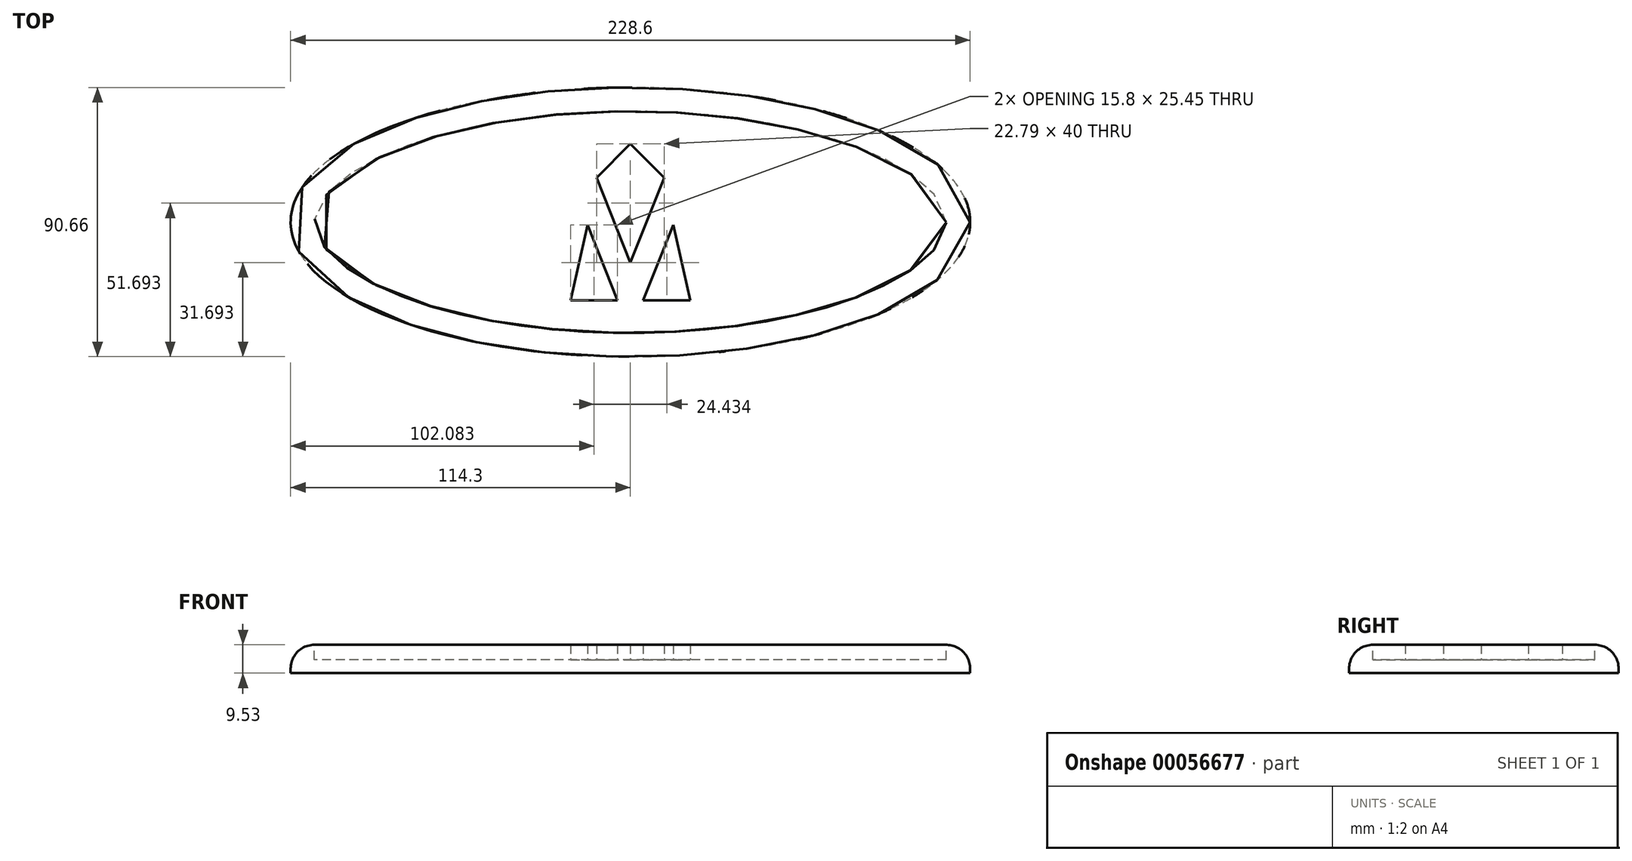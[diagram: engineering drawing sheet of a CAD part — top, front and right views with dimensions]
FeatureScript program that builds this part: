
annotation { "Feature Type Name" : "Feature", "Feature Type Description" : "" }
export const myFeature = defineFeature(function(context is Context, id is Id, definition is map)
    precondition{}
    {
        {
            var Q0;
            Q0=qCreatedBy(makeId("Top.planeOp"),FACE);
            var sketch = newSketch(context, id + "F0", { "sketchPlane" : qUnion([Q0])});
            skEllipse(sketch, "E0", {"center": v(0, 0) * mm, "majorRadius": 114.3 * mm, "minorRadius": 45.33 * mm, "majorAxis": v(1, 0)});
            skSolve(sketch);
        }
        {
            var Q0;
            Q0=makeQuery(id+"F0.imprint","IMPRINT",FACE,{"disambiguationData":[TD([[makeQuery(id+"F0.imprint","IMPRINT",EDGE,{"derivedFrom":sQuery(id+"F0.wireOp",EDGE,"E0")}),1.0]])]});
            extrude(context, id + "F1", {"entities" : qUnion([Q0]), "depth" : 9.52 * mm});
        }
        {
            var Q0;
            Q0=makeQuery(id+"F1.opExtrude","CAP_EDGE",EDGE,{"disambiguationData":[OSD([sQuery(id+"F0.wireOp",EDGE,"E0")])],"isStart":false});
            fillet(context, id + "F2", {"entities" : qUnion([Q0]), "radius" : 8 * mm, "tangentPropagation" : true, "allowEdgeOverflow" : false});
        }
        {
            var Q0;
            Q0=makeQuery(id+"F1.opExtrude","CAP_FACE",FACE,{"disambiguationData":[OSD([sQuery(id+"F0.wireOp",EDGE,"E0")])],"isStart":false});
            var sketch = newSketch(context, id + "F3", { "sketchPlane" : qUnion([Q0])});
            skLineSegment(sketch, "E1", {"start": v(14.45, -0.91) * mm, "end": v(20.12, -26.36) * mm});
            skLineSegment(sketch, "E2", {"start": v(20.12, -26.36) * mm, "end": v(4.31, -26.36) * mm});
            skLineSegment(sketch, "E3", {"start": v(4.31, -26.36) * mm, "end": v(14.45, -0.91) * mm});
            skLineSegment(sketch, "E4", {"start": v(-14.45, -0.91) * mm, "end": v(-4.31, -26.36) * mm});
            skLineSegment(sketch, "E5", {"start": v(-4.31, -26.36) * mm, "end": v(-20.12, -26.36) * mm});
            skLineSegment(sketch, "E6", {"start": v(-20.12, -26.36) * mm, "end": v(-14.45, -0.91) * mm});
            skLineSegment(sketch, "E7", {"start": v(0, 26.36) * mm, "end": v(11.4, 14.97) * mm});
            skLineSegment(sketch, "E8", {"start": v(11.4, 14.97) * mm, "end": v(0, -13.64) * mm});
            skLineSegment(sketch, "E9", {"start": v(-11.4, 14.97) * mm, "end": v(0, 26.36) * mm});
            skLineSegment(sketch, "E10", {"start": v(0, -13.64) * mm, "end": v(-11.4, 14.97) * mm});
            skPoint(sketch, "E11", {"position": v(-9.38, -13.64) * mm});
            skPoint(sketch, "E12", {"position": v(9.38, -13.64) * mm});
            skLineSegment(sketch, "E13", {"start": v(0, 26.36) * mm, "end": v(0, -26.36) * mm, "construction": true});
            skLineSegment(sketch, "E14", {"start": v(-4.31, -26.36) * mm, "end": v(0, -26.36) * mm, "construction": true});
            skLineSegment(sketch, "E15", {"start": v(4.31, -26.36) * mm, "end": v(0, -26.36) * mm, "construction": true});
            skPoint(sketch, "E16", {"position": v(0, 0) * mm});
            skSolve(sketch);
        }
        {
            var Q0;
            Q0=makeQuery(id+"F3.imprint","IMPRINT",FACE,{"disambiguationData":[TD([[makeQuery(id+"F3.imprint","IMPRINT",EDGE,{"derivedFrom":sQuery(id+"F3.wireOp",EDGE,"E1")}),1.0]])]});
            extrude(context, id + "F4", {"entities" : qUnion([Q0]), "operationType" : NewBodyOperationType.REMOVE, "oppositeDirection" : true, "depth" : 5 * mm});
        }
        {
            var Q0;
            Q0=makeQuery(id+"F4.boolean.opBoolean","COPY",FACE,{"derivedFrom":makeQuery(id+"F4.opExtrude","CAP_FACE",FACE,{"disambiguationData":[OSD([sQuery(id+"F0.wireOp",EDGE,"E0"),sQuery(id+"F3.wireOp",EDGE,"E1"),sQuery(id+"F3.wireOp",EDGE,"E2"),sQuery(id+"F3.wireOp",EDGE,"E3"),sQuery(id+"F3.wireOp",EDGE,"E4"),sQuery(id+"F3.wireOp",EDGE,"E5"),sQuery(id+"F3.wireOp",EDGE,"E6"),sQuery(id+"F3.wireOp",EDGE,"E7"),sQuery(id+"F3.wireOp",EDGE,"E8"),sQuery(id+"F3.wireOp",EDGE,"E9"),sQuery(id+"F3.wireOp",EDGE,"E10")])],"isStart":false})});
            var Q1;
            Q1=makeQuery(id+"F4.boolean.opBoolean","SPLIT",FACE,{"disambiguationData":[TD([makeQuery(id+"F4.opExtrude","SWEPT_FACE",FACE,{"disambiguationData":[OSD([sQuery(id+"F3.wireOp",EDGE,"E7")])]})])],"derivedFrom":makeQuery(id+"F1.opExtrude","CAP_FACE",FACE,{"disambiguationData":[OSD([sQuery(id+"F0.wireOp",EDGE,"E0")])],"isStart":false})});
            extrude(context, id + "F5", {"entities" : qUnion([Q0]), "endBound" : BoundingType.UP_TO_SURFACE, "endBoundEntityFace" : qUnion([Q1]), "depth" : 25 * mm});
        }
    });
